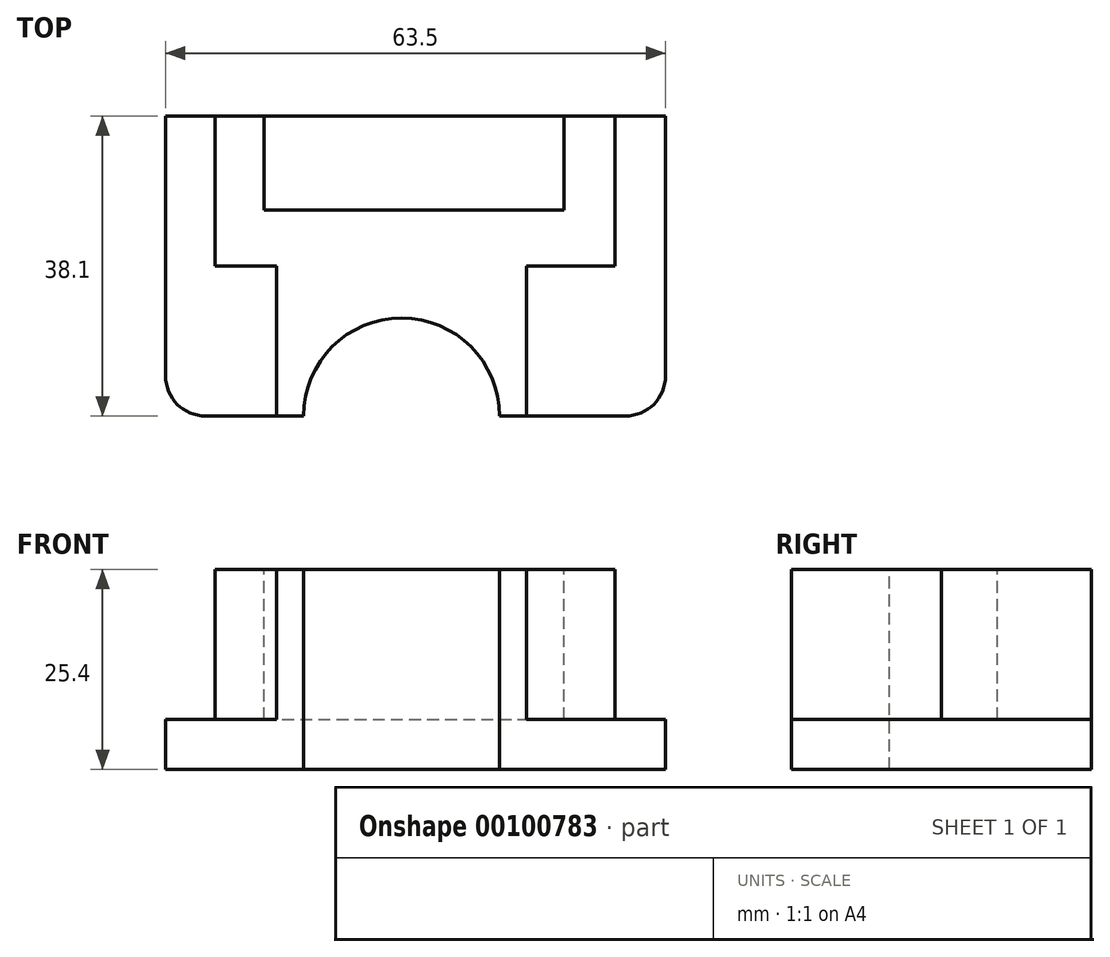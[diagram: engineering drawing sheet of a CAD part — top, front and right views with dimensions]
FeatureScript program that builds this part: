
annotation { "Feature Type Name" : "Feature", "Feature Type Description" : "" }
export const myFeature = defineFeature(function(context is Context, id is Id, definition is map)
    precondition{}
    {
        {
            var Q0;
            Q0=qCreatedBy(makeId("Top.planeOp"),FACE);
            var sketch = newSketch(context, id + "F0", { "sketchPlane" : qUnion([Q0])});
            skLineSegment(sketch, "E0.bottom", {"start": v(-31.75, 19.05) * mm, "end": v(31.75, 19.05) * mm});
            skLineSegment(sketch, "E0.top", {"start": v(-31.75, -19.05) * mm, "end": v(31.75, -19.05) * mm});
            skLineSegment(sketch, "E0.left", {"start": v(-31.75, 19.05) * mm, "end": v(-31.75, -19.05) * mm});
            skLineSegment(sketch, "E0.right", {"start": v(31.75, 19.05) * mm, "end": v(31.75, -19.05) * mm});
            skPoint(sketch, "E0.middle", {"position": v(0, 0) * mm});
            skSolve(sketch);
        }
        {
            var Q0;
            Q0 = qSketchRegion(id + "F0", true);
            extrude(context, id + "F1", {"entities" : qUnion([Q0]), "depth" : 6.35 * mm});
        }
        {
            var Q0;
            Q0=makeQuery(id+"F1.opExtrude","CAP_FACE",FACE,{"disambiguationData":[OSD([sQuery(id+"F0.wireOp",EDGE,"E0.bottom"),sQuery(id+"F0.wireOp",EDGE,"E0.top"),sQuery(id+"F0.wireOp",EDGE,"E0.left"),sQuery(id+"F0.wireOp",EDGE,"E0.right")])],"isStart":false});
            var sketch = newSketch(context, id + "F2", { "sketchPlane" : qUnion([Q0])});
            skLineSegment(sketch, "E1.bottom", {"start": v(-25.5, 19.05) * mm, "end": v(25.3, 19.05) * mm});
            skLineSegment(sketch, "E1.top", {"start": v(-25.5, 0) * mm, "end": v(25.3, 0) * mm});
            skLineSegment(sketch, "E1.left", {"start": v(-25.5, 19.05) * mm, "end": v(-25.5, 0) * mm});
            skLineSegment(sketch, "E1.right", {"start": v(25.3, 19.05) * mm, "end": v(25.3, 0) * mm});
            skSolve(sketch);
        }
        {
            var Q0;
            Q0 = qSketchRegion(id + "F2", true);
            extrude(context, id + "F3", {"entities" : qUnion([Q0]), "operationType" : NewBodyOperationType.ADD, "depth" : 19.05 * mm});
        }
        {
            var Q0;
            Q0=makeQuery(id+"F3.opExtrude","CAP_FACE",FACE,{"disambiguationData":[OSD([sQuery(id+"F2.wireOp",EDGE,"E1.bottom"),sQuery(id+"F2.wireOp",EDGE,"E1.top"),sQuery(id+"F2.wireOp",EDGE,"E1.left"),sQuery(id+"F2.wireOp",EDGE,"E1.right")])],"isStart":false});
            var sketch = newSketch(context, id + "F4", { "sketchPlane" : qUnion([Q0])});
            skLineSegment(sketch, "E2.bottom", {"start": v(-19.23, 19.05) * mm, "end": v(18.87, 19.05) * mm});
            skLineSegment(sketch, "E2.top", {"start": v(-19.23, 7.11) * mm, "end": v(18.87, 7.11) * mm});
            skLineSegment(sketch, "E2.left", {"start": v(-19.23, 19.05) * mm, "end": v(-19.23, 7.11) * mm});
            skLineSegment(sketch, "E2.right", {"start": v(18.87, 19.05) * mm, "end": v(18.87, 7.11) * mm});
            skSolve(sketch);
        }
        {
            var Q0;
            Q0 = qSketchRegion(id + "F4", true);
            extrude(context, id + "F5", {"entities" : qUnion([Q0]), "operationType" : NewBodyOperationType.REMOVE, "oppositeDirection" : true, "depth" : 19.05 * mm});
        }
        {
            var Q0;
            Q0=makeQuery(id+"F1.opExtrude","SWEPT_EDGE",EDGE,{"disambiguationData":[OSD([sQuery(id+"F0.wireOp",EDGE,"E0.top"),sQuery(id+"F0.wireOp",EDGE,"E0.left")])]});
            var Q1;
            Q1=makeQuery(id+"F1.opExtrude","SWEPT_EDGE",EDGE,{"disambiguationData":[OSD([sQuery(id+"F0.wireOp",EDGE,"E0.top"),sQuery(id+"F0.wireOp",EDGE,"E0.right")])]});
            fillet(context, id + "F6", {"entities" : qUnion([Q0, Q1]), "radius" : 5.08 * mm, "tangentPropagation" : true, "allowEdgeOverflow" : false});
        }
        {
            var Q0;
            Q0=makeQuery(id+"F1.opExtrude","CAP_FACE",FACE,{"disambiguationData":[OSD([sQuery(id+"F0.wireOp",EDGE,"E0.bottom"),sQuery(id+"F0.wireOp",EDGE,"E0.top"),sQuery(id+"F0.wireOp",EDGE,"E0.left"),sQuery(id+"F0.wireOp",EDGE,"E0.right")])],"isStart":false});
            var sketch = newSketch(context, id + "F7", { "sketchPlane" : qUnion([Q0])});
            skLineSegment(sketch, "E3.bottom", {"start": v(-17.65, 0) * mm, "end": v(14.1, 0) * mm});
            skLineSegment(sketch, "E3.top", {"start": v(-17.65, -19.05) * mm, "end": v(14.1, -19.05) * mm});
            skLineSegment(sketch, "E3.left", {"start": v(-17.65, 0) * mm, "end": v(-17.65, -19.05) * mm});
            skLineSegment(sketch, "E3.right", {"start": v(14.1, 0) * mm, "end": v(14.1, -19.05) * mm});
            skSolve(sketch);
        }
        {
            var Q0;
            Q0 = qSketchRegion(id + "F7", true);
            extrude(context, id + "F8", {"entities" : qUnion([Q0]), "operationType" : NewBodyOperationType.ADD, "depth" : 19.05 * mm});
        }
        {
            var Q0;
            Q0=makeQuery(id+"F8.boolean.opBoolean","MERGE",FACE,{"derivedFrom":[makeQuery(id+"F3.opExtrude","CAP_FACE",FACE,{"disambiguationData":[OSD([sQuery(id+"F2.wireOp",EDGE,"E1.bottom"),sQuery(id+"F2.wireOp",EDGE,"E1.top"),sQuery(id+"F2.wireOp",EDGE,"E1.left"),sQuery(id+"F2.wireOp",EDGE,"E1.right")])],"isStart":false}),makeQuery(id+"F8.opExtrude","CAP_FACE",FACE,{"disambiguationData":[OSD([sQuery(id+"F7.wireOp",EDGE,"E3.bottom"),sQuery(id+"F7.wireOp",EDGE,"E3.top"),sQuery(id+"F7.wireOp",EDGE,"E3.left"),sQuery(id+"F7.wireOp",EDGE,"E3.right")])],"isStart":false})]});
            var sketch = newSketch(context, id + "F9", { "sketchPlane" : qUnion([Q0])});
            skCircle(sketch, "E4", {"center": v(-1.77, -19.05) * mm, "radius": 12.45 * mm});
            skSolve(sketch);
        }
        {
            var Q0;
            Q0 = qSketchRegion(id + "F9", true);
            extrude(context, id + "F10", {"entities" : qUnion([Q0]), "operationType" : NewBodyOperationType.REMOVE, "endBound" : BoundingType.THROUGH_ALL, "oppositeDirection" : true, "depth" : 25.4 * mm});
        }
    });
